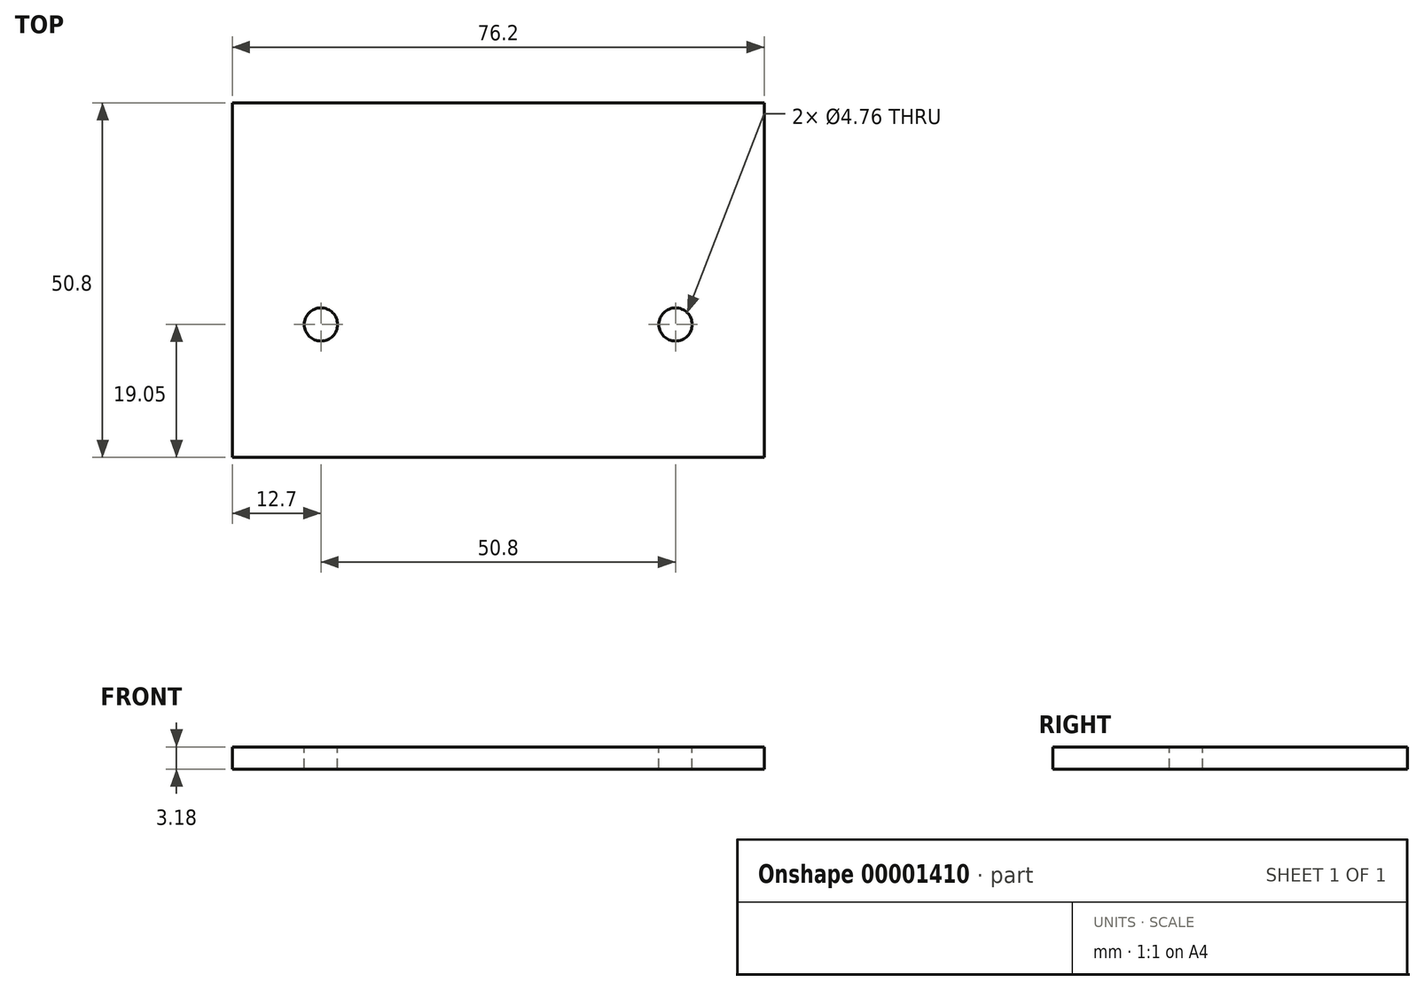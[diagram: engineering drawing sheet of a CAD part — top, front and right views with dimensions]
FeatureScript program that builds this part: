
annotation { "Feature Type Name" : "Feature", "Feature Type Description" : "" }
export const myFeature = defineFeature(function(context is Context, id is Id, definition is map)
    precondition{}
    {
        {
            var Q0;
            Q0=qCreatedBy(makeId("Top.planeOp"),FACE);
            var sketch = newSketch(context, id + "F0", { "sketchPlane" : qUnion([Q0])});
            skLineSegment(sketch, "E0.rect.bottom", {"start": v(38.1, 25.4) * mm, "end": v(-38.1, 25.4) * mm});
            skLineSegment(sketch, "E0.rect.top", {"start": v(38.1, -25.4) * mm, "end": v(-38.1, -25.4) * mm});
            skLineSegment(sketch, "E0.rect.left", {"start": v(38.1, 25.4) * mm, "end": v(38.1, -25.4) * mm});
            skLineSegment(sketch, "E0.rect.right", {"start": v(-38.1, 25.4) * mm, "end": v(-38.1, -25.4) * mm});
            skPoint(sketch, "E0.rect.middle", {"position": v(0, 0) * mm});
            skSolve(sketch);
        }
        {
            var Q0;
            Q0 = qSketchRegion(id + "F0", true);
            extrude(context, id + "F1", {"entities" : qUnion([Q0]), "endBound" : BoundingType.SYMMETRIC, "depth" : 3.17 * mm});
        }
        {
            var Q0;
            Q0=makeQuery(id+"F1.opExtrude","CAP_FACE",FACE,{"disambiguationData":[OSD([sQuery(id+"F0.wireOp",EDGE,"E0.rect.bottom"),sQuery(id+"F0.wireOp",EDGE,"E0.rect.top"),sQuery(id+"F0.wireOp",EDGE,"E0.rect.left"),sQuery(id+"F0.wireOp",EDGE,"E0.rect.right")])],"isStart":false});
            var sketch = newSketch(context, id + "F2", { "sketchPlane" : qUnion([Q0])});
            skCircle(sketch, "E1", {"center": v(-25.4, -6.35) * mm, "radius": 2.38 * mm});
            skCircle(sketch, "E2", {"center": v(25.4, -6.35) * mm, "radius": 2.38 * mm});
            skSolve(sketch);
        }
        {
            var Q0;
            Q0 = qSketchRegion(id + "F2", true);
            extrude(context, id + "F3", {"entities" : qUnion([Q0]), "operationType" : NewBodyOperationType.REMOVE, "endBound" : BoundingType.THROUGH_ALL, "oppositeDirection" : true, "depth" : 25.4 * mm});
        }
    });
